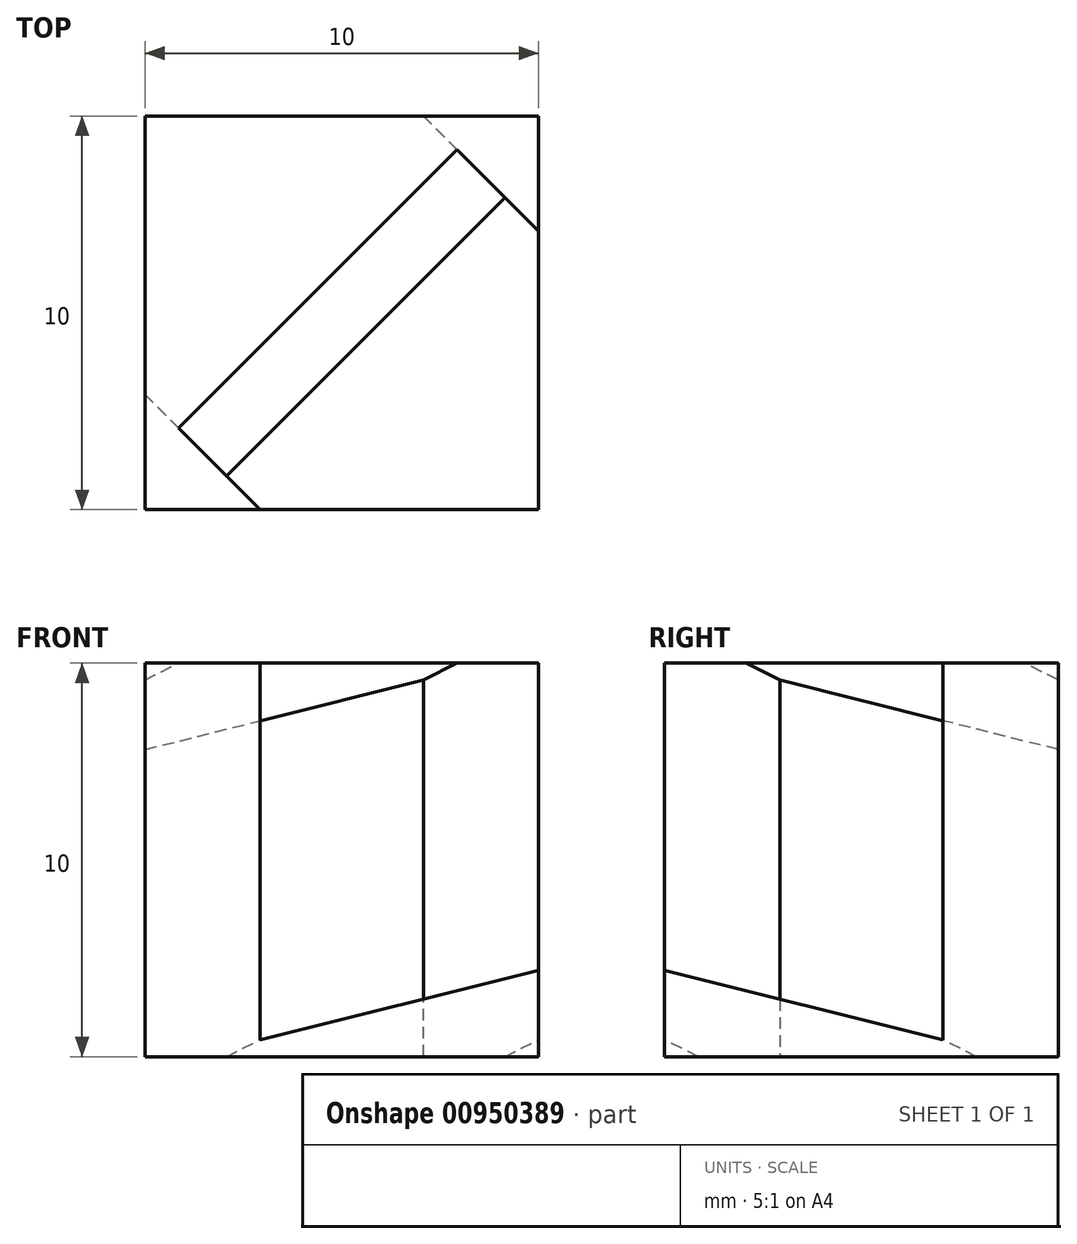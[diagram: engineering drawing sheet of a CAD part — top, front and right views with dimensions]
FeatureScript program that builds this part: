
annotation { "Feature Type Name" : "Feature", "Feature Type Description" : "" }
export const myFeature = defineFeature(function(context is Context, id is Id, definition is map)
    precondition{}
    {
        {
            var Q0;
            Q0=qCreatedBy(makeId("Top.planeOp"),FACE);
            var sketch = newSketch(context, id + "F0", { "sketchPlane" : qUnion([Q0])});
            skLineSegment(sketch, "E0.bottom", {"start": v(5, -5) * mm, "end": v(-5, -5) * mm});
            skLineSegment(sketch, "E0.top", {"start": v(5, 5) * mm, "end": v(-5, 5) * mm});
            skLineSegment(sketch, "E0.left", {"start": v(5, -5) * mm, "end": v(5, 5) * mm});
            skLineSegment(sketch, "E0.right", {"start": v(-5, -5) * mm, "end": v(-5, 5) * mm});
            skPoint(sketch, "E0.middle", {"position": v(0, 0) * mm});
            skSolve(sketch);
        }
        {
            var Q0;
            Q0=makeQuery(id+"F0.imprint","IMPRINT",FACE,{"disambiguationData":[TD([[makeQuery(id+"F0.imprint","IMPRINT",EDGE,{"derivedFrom":sQuery(id+"F0.wireOp",EDGE,"E0.bottom")}),-1.0]])]});
            extrude(context, id + "F1", {"entities" : qUnion([Q0]), "depth" : 10 * mm, "offsetDistance" : 25 * mm});
        }
        {
            var Q0;
            Q0=makeQuery(id+"F1.opExtrude","CAP_FACE",FACE,{"disambiguationData":[OSD([sQuery(id+"F0.wireOp",EDGE,"E0.bottom"),sQuery(id+"F0.wireOp",EDGE,"E0.top"),sQuery(id+"F0.wireOp",EDGE,"E0.left"),sQuery(id+"F0.wireOp",EDGE,"E0.right")])],"isStart":false});
            var sketch = newSketch(context, id + "F2", { "sketchPlane" : qUnion([Q0])});
            skLineSegment(sketch, "E1", {"start": v(-5, -2.5) * mm, "end": v(2.5, 5) * mm});
            skSolve(sketch);
        }
        {
            var Q0;
            Q0=makeQuery(id+"F1.opExtrude","CAP_FACE",FACE,{"disambiguationData":[OSD([sQuery(id+"F0.wireOp",EDGE,"E0.bottom"),sQuery(id+"F0.wireOp",EDGE,"E0.top"),sQuery(id+"F0.wireOp",EDGE,"E0.left"),sQuery(id+"F0.wireOp",EDGE,"E0.right")])],"isStart":true});
            var sketch = newSketch(context, id + "F3", { "sketchPlane" : qUnion([Q0])});
            skLineSegment(sketch, "E2", {"start": v(-2.5, 5) * mm, "end": v(5, -2.5) * mm});
            skSolve(sketch);
        }
        {
            var Q0;
            Q0=sQuery(id+"F2.wireOp",EDGE,"E1");
            var Q1;
            Q1=sQuery(id+"F3.wireOp",EDGE,"E2");
            cPlane(context, id + "F4", {"entities" : qUnion([Q0, Q1]), "cplaneType" : CPlaneType.LINE_ANGLE, "offset" : 25 * mm, "angle" : 0 * degree, "oppositeDirection" : true, "width" : 150 * mm, "height" : 150 * mm});
        }
        {
            var Q0;
            Q0=qCreatedBy(id+"F4.planeOp",FACE);
            var sketch = newSketch(context, id + "F5", { "sketchPlane" : qUnion([Q0])});
            skLineSegment(sketch, "E3.0", {"start": v(8.2, 7.83) * mm, "end": v(-1.86, 11.18) * mm, "construction": true});
            skLineSegment(sketch, "E4.0", {"start": v(4.84, -2.24) * mm, "end": v(-5.22, 1.12) * mm, "construction": true});
            skLineSegment(sketch, "E5", {"start": v(4.84, -2.24) * mm, "end": v(8.2, 7.83) * mm, "construction": true});
            skLineSegment(sketch, "E6", {"start": v(-5.22, 1.12) * mm, "end": v(-1.86, 11.18) * mm, "construction": true});
            skLineSegment(sketch, "E7.0", {"start": v(4.65, -1.85) * mm, "end": v(7.82, 7.63) * mm});
            skLineSegment(sketch, "E7.1", {"start": v(4.65, -1.85) * mm, "end": v(-4.83, 1.3) * mm});
            skLineSegment(sketch, "E7.2", {"start": v(-4.83, 1.3) * mm, "end": v(-1.67, 10.8) * mm});
            skLineSegment(sketch, "E7.3", {"start": v(7.82, 7.63) * mm, "end": v(-1.67, 10.8) * mm});
            skSolve(sketch);
        }
        {
            var Q0;
            Q0 = qSketchRegion(id + "F5", true);
            extrude(context, id + "F6", {"entities" : qUnion([Q0]), "operationType" : NewBodyOperationType.REMOVE, "endBound" : BoundingType.THROUGH_ALL, "depth" : 25 * mm, "offsetDistance" : 25 * mm, "hasSecondDirection" : true, "secondDirectionBound" : SecondDirectionBoundingType.THROUGH_ALL, "secondDirectionOppositeDirection" : true, "secondDirectionDepth" : 25 * mm});
        }
    });
